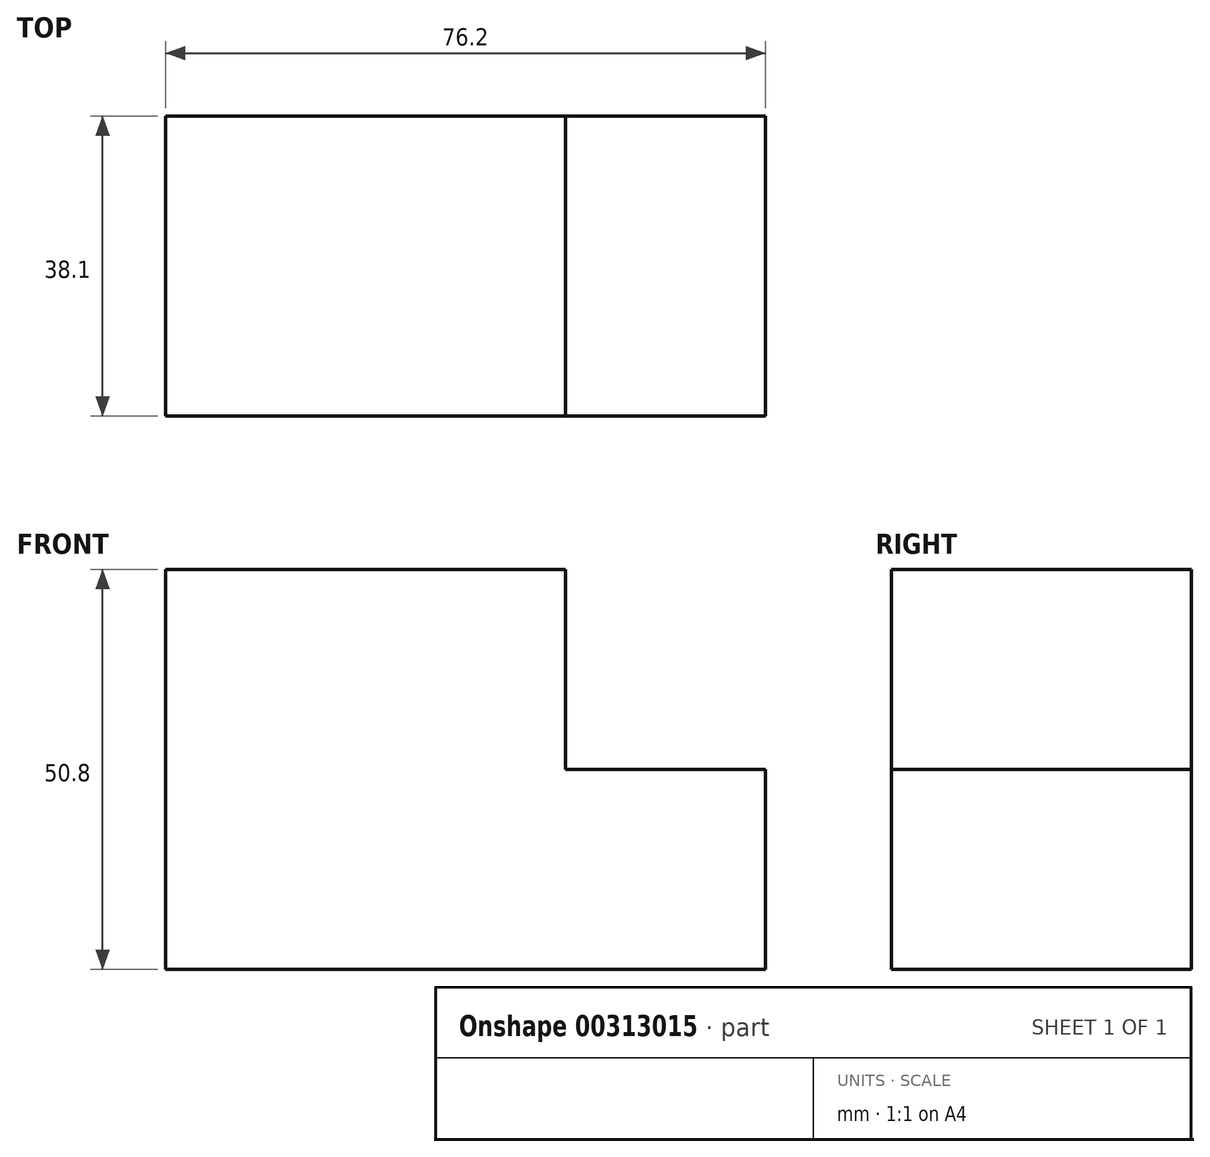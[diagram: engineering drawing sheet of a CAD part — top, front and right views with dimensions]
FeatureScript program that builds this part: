
annotation { "Feature Type Name" : "Feature", "Feature Type Description" : "" }
export const myFeature = defineFeature(function(context is Context, id is Id, definition is map)
    precondition{}
    {
        {
            var Q0;
            Q0=qCreatedBy(makeId("Front.planeOp"),FACE);
            var sketch = newSketch(context, id + "F0", { "sketchPlane" : qUnion([Q0])});
            skLineSegment(sketch, "E0", {"start": v(-44.48, 1.32) * mm, "end": v(31.72, 1.32) * mm});
            skLineSegment(sketch, "E1", {"start": v(31.72, 1.32) * mm, "end": v(31.72, 26.72) * mm});
            skLineSegment(sketch, "E2", {"start": v(31.72, 26.72) * mm, "end": v(6.32, 26.72) * mm});
            skLineSegment(sketch, "E3", {"start": v(6.32, 26.72) * mm, "end": v(6.32, 52.12) * mm});
            skLineSegment(sketch, "E4", {"start": v(-44.48, 52.12) * mm, "end": v(-44.48, 1.32) * mm});
            skLineSegment(sketch, "E5", {"start": v(-44.48, 52.12) * mm, "end": v(6.32, 52.12) * mm});
            skSolve(sketch);
        }
        {
            var Q0;
            Q0=makeQuery(id+"F0.imprint","IMPRINT",FACE,{"disambiguationData":[TD([[makeQuery(id+"F0.imprint","IMPRINT",EDGE,{"derivedFrom":sQuery(id+"F0.wireOp",EDGE,"E0")}),1.0]])]});
            extrude(context, id + "F1", {"entities" : qUnion([Q0]), "depth" : 38.1 * mm});
        }
    });
